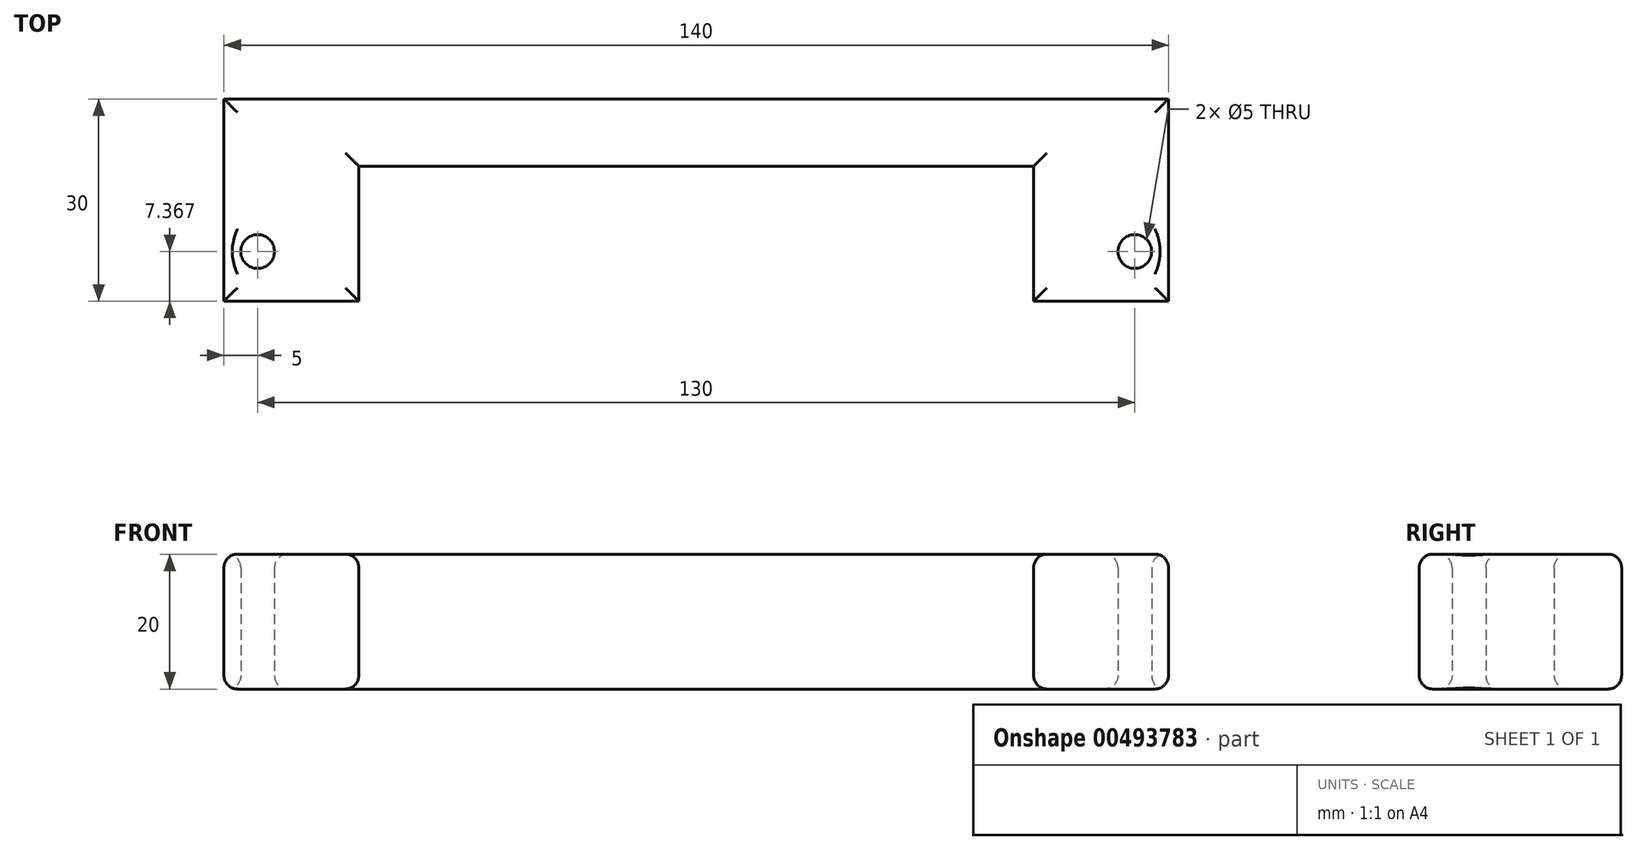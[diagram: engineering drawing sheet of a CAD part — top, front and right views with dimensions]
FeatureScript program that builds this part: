
annotation { "Feature Type Name" : "Feature", "Feature Type Description" : "" }
export const myFeature = defineFeature(function(context is Context, id is Id, definition is map)
    precondition{}
    {
        {
            var Q0;
            Q0=qCreatedBy(makeId("Top.planeOp"),FACE);
            var sketch = newSketch(context, id + "F0", { "sketchPlane" : qUnion([Q0])});
            skLineSegment(sketch, "E0", {"start": v(0, 30) * mm, "end": v(0, 20) * mm});
            skLineSegment(sketch, "E1", {"start": v(0, 20) * mm, "end": v(50, 20) * mm});
            skLineSegment(sketch, "E2", {"start": v(50, 20) * mm, "end": v(50, 0) * mm});
            skLineSegment(sketch, "E3", {"start": v(50, 0) * mm, "end": v(70, 0) * mm});
            skLineSegment(sketch, "E4", {"start": v(70, 0) * mm, "end": v(70, 30) * mm});
            skLineSegment(sketch, "E5", {"start": v(0, 30) * mm, "end": v(70, 30) * mm});
            skSolve(sketch);
        }
        {
            var Q0;
            Q0 = qSketchRegion(id + "F0", true);
            extrude(context, id + "F1", {"entities" : qUnion([Q0]), "depth" : 20 * mm});
        }
        {
            var Q0;
            Q0=qCreatedBy(makeId("Top.planeOp"),FACE);
            var sketch = newSketch(context, id + "F2", { "sketchPlane" : qUnion([Q0])});
            skPoint(sketch, "E6", {"position": v(65, 7.37) * mm});
            skSolve(sketch);
        }
        {
            var Q0;
            Q0=sQuery(id+"F2.wireOp",VERTEX,"E6");
            var Q1;
            Q1=makeQuery(id+"F1.opExtrude","SWEPT_BODY",BODY,{"disambiguationData":[OSD([sQuery(id+"F0.wireOp",EDGE,"E0"),sQuery(id+"F0.wireOp",EDGE,"E1"),sQuery(id+"F0.wireOp",EDGE,"E2"),sQuery(id+"F0.wireOp",EDGE,"E3"),sQuery(id+"F0.wireOp",EDGE,"E4"),sQuery(id+"F0.wireOp",EDGE,"E5")])]});
            hole(context, id + "F3", {"style" : HoleStyle.SIMPLE, "endStyle" : HoleEndStyle.THROUGH, "oppositeDirection" : true, "holeDiameter" : 5 * mm, "isTappedThrough" : true, "tappedDepth" : 12 * mm, "tapClearance" : 3, "locations" : qUnion([Q0]), "scope" : qUnion([Q1])});
        }
        {
            var Q0;
            Q0=makeQuery(id+"F1.opExtrude","SWEPT_BODY",BODY,{"disambiguationData":[OSD([sQuery(id+"F0.wireOp",EDGE,"E0"),sQuery(id+"F0.wireOp",EDGE,"E1"),sQuery(id+"F0.wireOp",EDGE,"E2"),sQuery(id+"F0.wireOp",EDGE,"E3"),sQuery(id+"F0.wireOp",EDGE,"E4"),sQuery(id+"F0.wireOp",EDGE,"E5")])]});
            var Q1;
            Q1=makeQuery(id+"F1.opExtrude","SWEPT_FACE",FACE,{"disambiguationData":[OSD([sQuery(id+"F0.wireOp",EDGE,"E0")])]});
            mirror(context, id + "F4", {"operationType" : NewBodyOperationType.ADD, "entities" : qUnion([Q0]), "mirrorPlane" : qUnion([Q1])});
        }
        {
            var Q0;
            {var subQ0=makeQuery(id+"F1.opExtrude","CAP_FACE",FACE,{"disambiguationData":[OSD([sQuery(id+"F0.wireOp",EDGE,"E0"),sQuery(id+"F0.wireOp",EDGE,"E1"),sQuery(id+"F0.wireOp",EDGE,"E2"),sQuery(id+"F0.wireOp",EDGE,"E3"),sQuery(id+"F0.wireOp",EDGE,"E4"),sQuery(id+"F0.wireOp",EDGE,"E5")])],"isStart":false});Q0=makeQuery(id+"F4.boolean.opBoolean","MERGE",FACE,{"derivedFrom":[subQ0,makeQuery(id+"F4.opPattern","COPY",FACE,{"derivedFrom":subQ0,"instanceName":"1"})]});}
            var Q1;
            {var subQ0=makeQuery(id+"F1.opExtrude","CAP_FACE",FACE,{"disambiguationData":[OSD([sQuery(id+"F0.wireOp",EDGE,"E0"),sQuery(id+"F0.wireOp",EDGE,"E1"),sQuery(id+"F0.wireOp",EDGE,"E2"),sQuery(id+"F0.wireOp",EDGE,"E3"),sQuery(id+"F0.wireOp",EDGE,"E4"),sQuery(id+"F0.wireOp",EDGE,"E5")])],"isStart":true});Q1=makeQuery(id+"F4.boolean.opBoolean","MERGE",FACE,{"derivedFrom":[subQ0,makeQuery(id+"F4.opPattern","COPY",FACE,{"derivedFrom":subQ0,"instanceName":"1"})]});}
            fillet(context, id + "F5", {"entities" : qUnion([Q0, Q1]), "radius" : 2 * mm, "tangentPropagation" : true, "allowEdgeOverflow" : false});
        }
    });
